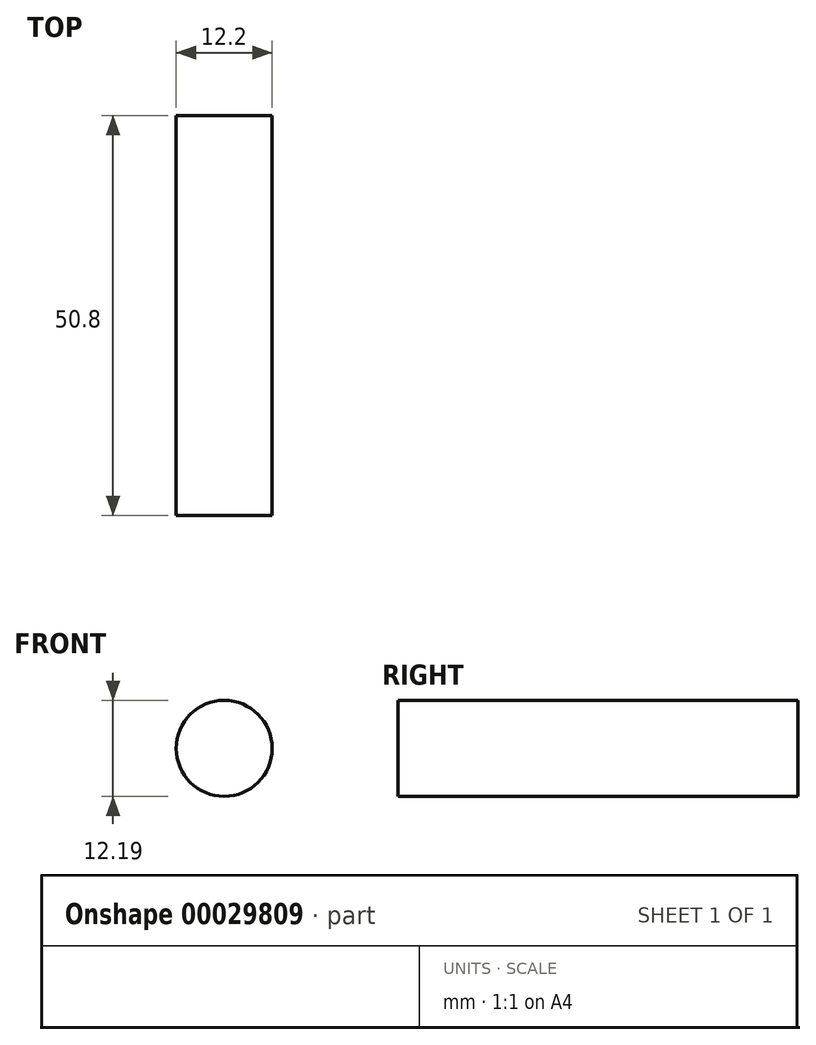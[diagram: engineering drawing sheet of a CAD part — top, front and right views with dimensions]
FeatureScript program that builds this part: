
annotation { "Feature Type Name" : "Feature", "Feature Type Description" : "" }
export const myFeature = defineFeature(function(context is Context, id is Id, definition is map)
    precondition{}
    {
        {
            var Q0;
            Q0=qCreatedBy(makeId("Front.planeOp"),FACE);
            var sketch = newSketch(context, id + "F0", { "sketchPlane" : qUnion([Q0])});
            skCircle(sketch, "E0", {"center": v(0, -1.48) * mm, "radius": 6.1 * mm});
            skSolve(sketch);
        }
        {
            var Q0;
            Q0=makeQuery(id+"F0.imprint","IMPRINT",FACE,{"disambiguationData":[TD([[makeQuery(id+"F0.imprint","IMPRINT",EDGE,{"derivedFrom":sQuery(id+"F0.wireOp",EDGE,"E0")}),1.0]])]});
            extrude(context, id + "F1", {"entities" : qUnion([Q0]), "depth" : 50.8 * mm});
        }
    });
